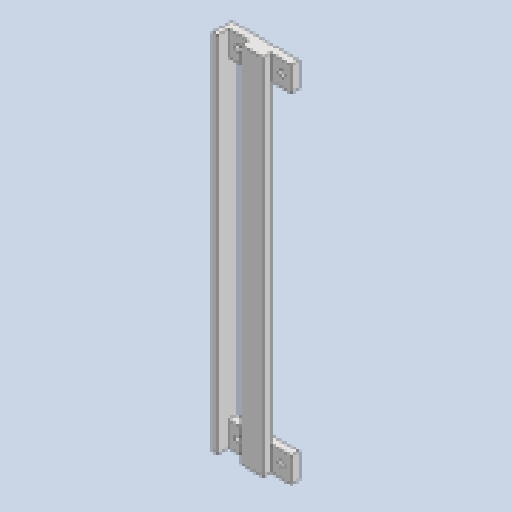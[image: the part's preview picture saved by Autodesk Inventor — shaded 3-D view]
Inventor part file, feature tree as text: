
AUTODESK INVENTOR PART (.ipt)
format: ipt  version: 2023 (Build 270158000, 158)  size: 209,920 bytes
history: native  units: mm
features: other x6, extrude x5, thicken_offset x5, sketch x5, projected_geometry x3, reference x2, plane x1, pattern_linear x1
ambient origin geometry x8: Origin, YZ Plane, XZ Plane, XY Plane, X Axis, Y Axis, Z Axis, Center Point
bodies: Solid1 (feature_tree)
feature tree (28):
  extrude  "Extrusion1"  Depth=2.0mm
  extrude  "Extrusion2"  Depth=2.0mm
  extrude  "Extrusion3"  Depth=7.0mm
  thicken_offset  "Thicken1"
  thicken_offset  "Thicken2"
  thicken_offset  "Thicken3"
  thicken_offset  "Thicken4"
  thicken_offset  "Thicken5"
  extrude  "Extrusion4"  Depth=4.0mm TaperAngle=0.0deg
  plane  "Work Plane1"
  extrude  "Extrusion5"  Depth=1.0mm
  pattern_linear  "Rectangular Pattern1"  Spacing1=1.0mm  [1 undecoded]
  sketch  "Sketch1"  dims[d0=2.0mm d1=2.0mm]
  reference  "Reference1"
  reference  "Reference2"
  sketch  "Sketch2"  dims[d2=2.0mm d3=2.0mm]
  sketch  "Sketch3"  dims[d4=2.0mm d5=0.0mm d6=7.0mm]
  projected_geometry  "Projected Loop1"
  sketch  "Sketch4"  dims[d7=117.0mm d8=4.0mm d9=0.0mm]
  projected_geometry  "Projected Loop2"
  projected_geometry  "Projected Loop3"
  sketch  "Sketch5"  dims[d10=2.0mm d11=0.0mm d12=1.0mm d13=1.0mm d14=0.5mm d15=0.5mm d16=0.5mm d17=0.5mm d18=0.5mm d19=0.5mm d20=0.5mm d21=0.5mm d22=6.0mm d23=117.0mm d24=2.0mm d25=0.0mm d26=2.0mm d27=0.0mm d28=20.0mm d30=30.0mm d31=20.0mm d33=30.0mm]
  parser-record x1  (decoder bookkeeping rows leaked as tree rows — omitted from the tree; the rows remain in map.json)
  other  "body_8d_wid_1.iam"
  other  "leg_1_2d_MIR:1"
  other  "leg_holder_2_MIR:1"
  other  "leg_2d_1:1"
  other  "leg_holder_2:1"
note: 1 required parameter value undecoded (feature->parameter linkage not recoverable at this tier; creation-order binding heuristic only, values carry confidence <= 0.55)
note: 1 file-system path scrubbed to <path> (originals preserved in map.json)
